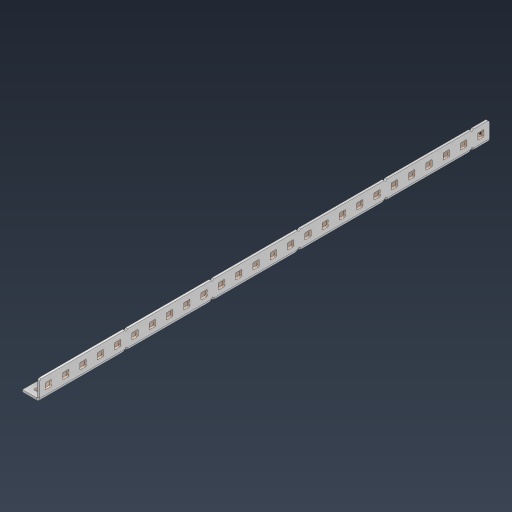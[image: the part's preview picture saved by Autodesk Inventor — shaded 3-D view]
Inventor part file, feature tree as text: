
AUTODESK INVENTOR PART (.ipt)
format: ipt  version: 2024.3 (Build 283343000, 343)  size: 1,030,656 bytes
history: native  units: in
note: dims shown in document units (in); Inventor stores cm internally (conversion verified against a paired STEP export)
features: other x85, extrude x76, sheet_metal_op x11, pattern_linear x2, mirror x1, chamfer x1, sketch x1
ambient origin geometry x8: Origin, YZ Plane, XZ Plane, XY Plane, X Axis, Y Axis, Z Axis, Center Point
bodies: Solid1 (feature_tree), Body (feature_tree)
feature tree (177):
  sheet_metal_op  "Flanges"
  other  "Flange Pattern Plane"
  other  "Flange Pattern Sketch"
  sheet_metal_op  "Flange Pattern"
  sheet_metal_op  "Body Pattern"
  pattern_linear  "Center Pattern"  Spacing1=13.0in  [1 undecoded]
  other  "Arc Length"
  mirror  "Notch Mirror"
  pattern_linear  "Notch Pattern"  Spacing1=0.0625in  [1 undecoded]
  chamfer  "End Chamfer"
  extrude  "Half Cut"  Depth=0.0625in
  other  "Plate1"
  sketch  "Sketch2"  dims[d0=1.0in d1=13.0in d2=0.0625in d3=0.0625in d4=0.0312in d5=0.125in d6=0.0625in d7=0.5in d8=90.0deg d9=0.0312in d10=0.25in d11=0.0625in d12=0.0625in d16=0.182in d17=0.02in d18=0.0625in d19=0.0in d20=0.25in d21=0.25in d38=10.2362in d40=0.5in d41=0.3937in d43=1.0in d46=0.172in d47=1.0in d48=0.0in d49=0.182in d50=0.02in d51=0.25in d52=0.25in d53=0.0625in d54=0.0in d55=0.172in d56=1.0in d57=0.0in d58=0.25in d60=10.2362in d62=0.5in d63=0.3937in d65=0.5in d85=0.1473in d86=0.1782in d88=0.04in d89=0.0625in d90=0.0in d91=0.04in d92=0.0491in d95=2.5in d96=0.04in d97=0.25in d98=45.0deg d99=0.25in d100=0.5in d101=0.0in d102=2.497in d106=0.182in d107=0.02in d108=0.5in d109=0.5in d110=0.0625in d111=0.0in d112=0.172in d113=0.5in d114=0.0in d117=0.5in d118=0.5in d119=0.5in]
  other  "Plate2"
  sheet_metal_op  "Bend1"
  sheet_metal_op  "Corner1"
  other  "Srf1"
  other  "Srf2"
  other  "Srf91"
  sheet_metal_op  "Body Pattern Sketch"
  other  "Srf92"
  other  "Srf786"
  other  "Srf823"
  other  "Srf824"
  other  "Srf825"
  other  "Srf826"
  other  "Srf827"
  other  "Srf828"
  other  "Srf829"
  other  "Srf856"
  other  "Srf857"
  other  "Srf858"
  other  "Srf859"
  other  "Srf860"
  other  "Srf861"
  other  "Srf862"
  other  "Srf889"
  other  "Srf890"
  other  "Srf891"
  other  "Srf892"
  other  "Srf893"
  other  "Srf894"
  other  "Srf895"
  other  "Srf896"
  other  "Srf922"
  other  "Srf923"
  other  "Srf924"
  other  "Srf925"
  other  "Srf926"
  other  "Srf959"
  other  "Srf960"
  other  "Srf961"
  other  "Srf962"
  other  "Srf963"
  other  "Srf996"
  other  "Srf997"
  other  "Srf998"
  other  "Srf999"
  other  "Srf1000"
  other  "Srf1143"
  other  "Srf1144"
  other  "Srf1145"
  other  "Srf1146"
  other  "Srf1147"
  other  "Srf1148"
  other  "Srf1149"
  other  "Srf1150"
  other  "Srf1151"
  other  "Srf1152"
  other  "Srf1153"
  other  "Srf1154"
  other  "Srf1199"
  other  "Srf1200"
  other  "Srf1201"
  other  "Srf1202"
  other  "Srf1203"
  other  "Srf1204"
  other  "Srf1205"
  other  "Srf1206"
  other  "Srf1207"
  other  "Srf1208"
  other  "Srf1209"
  other  "Srf1210"
  other  "Srf1255"
  other  "Srf1256"
  other  "Srf1257"
  other  "Srf1258"
  other  "Srf1259"
  other  "Srf1260"
  other  "Srf1261"
  other  "Srf1262"
  other  "Srf1263"
  other  "Srf1264"
  other  "Srf1265"
  other  "Srf1266"
  sheet_metal_op  "Flange Stamp"
  sheet_metal_op  "Flange Circle"
  sheet_metal_op  "Body Stamp"
  sheet_metal_op  "Body Circle"
  other  "Center Stamp"
  other  "Center Circle"
  sheet_metal_op  "Notch"
  extrude  "ExtrusionSrf2"  Depth=0.0312in
  extrude  "ExtrusionSrf92"  Depth=0.5in
  extrude  "ExtrusionSrf823"  Depth=0.0625in
  extrude  "ExtrusionSrf824"  Depth=0.5in TaperAngle=90.0deg
  extrude  "ExtrusionSrf825"  Depth=0.25in
  extrude  "ExtrusionSrf826"  Depth=0.0625in
  extrude  "ExtrusionSrf827"  Depth=0.0625in
  extrude  "ExtrusionSrf828"  Depth=0.182in
  extrude  "ExtrusionSrf829"  Depth=0.02in
  extrude  "ExtrusionSrf856"  Depth=0.0625in
  extrude  "ExtrusionSrf857"  TaperAngle=0.0deg  [1 undecoded]
  extrude  "ExtrusionSrf858"  Depth=0.25in
  extrude  "ExtrusionSrf859"  Depth=0.25in
  extrude  "ExtrusionSrf860"  Depth=0.5in
  extrude  "ExtrusionSrf861"  Depth=0.5in
  extrude  "ExtrusionSrf862"  Depth=1.0in TaperAngle=0.0deg
  extrude  "ExtrusionSrf889"  Depth=0.182in
  extrude  "ExtrusionSrf890"  Depth=0.02in
  extrude  "ExtrusionSrf891"  Depth=0.25in
  extrude  "ExtrusionSrf892"  Depth=0.25in
  extrude  "ExtrusionSrf893"  Depth=0.0625in
  extrude  "ExtrusionSrf894"  TaperAngle=0.0deg  [1 undecoded]
  extrude  "ExtrusionSrf895"  Depth=0.5in
  extrude  "ExtrusionSrf896"  Depth=1.0in TaperAngle=0.0deg
  extrude  "ExtrusionSrf922"  Depth=0.25in
  extrude  "ExtrusionSrf923"  Depth=0.5in
  extrude  "ExtrusionSrf924"  Depth=0.5in
  extrude  "ExtrusionSrf925"  Depth=0.5in
  extrude  "ExtrusionSrf926"  Depth=0.5in
  extrude  "ExtrusionSrf959"  Depth=0.5in
  extrude  "ExtrusionSrf960"  Depth=0.0625in
  extrude  "ExtrusionSrf961"  TaperAngle=0.0deg  [1 undecoded]
  extrude  "ExtrusionSrf962"  Depth=0.5in
  extrude  "ExtrusionSrf963"  Depth=0.5in
  extrude  "ExtrusionSrf996"  Depth=2.5in
  extrude  "ExtrusionSrf997"  Depth=0.25in TaperAngle=45.0deg
  extrude  "ExtrusionSrf998"  Depth=0.25in
  extrude  "ExtrusionSrf999"  Depth=0.5in TaperAngle=0.0deg
  extrude  "ExtrusionSrf1000"  Depth=0.5in
  extrude  "ExtrusionSrf1143"  Depth=0.182in
  extrude  "ExtrusionSrf1144"  Depth=0.02in
  extrude  "ExtrusionSrf1145"  Depth=0.5in
  extrude  "ExtrusionSrf1146"  Depth=0.5in
  extrude  "ExtrusionSrf1147"  Depth=0.0625in
  extrude  "ExtrusionSrf1148"  TaperAngle=0.0deg  [1 undecoded]
  extrude  "ExtrusionSrf1149"  Depth=0.5in
  extrude  "ExtrusionSrf1150"  Depth=0.5in TaperAngle=0.0deg
  extrude  "ExtrusionSrf1151"  Depth=0.5in
  extrude  "ExtrusionSrf1152"  Depth=0.5in
  extrude  "ExtrusionSrf1153"  Depth=0.5in
  extrude  "ExtrusionSrf1154"  [1 undecoded]
  extrude  "ExtrusionSrf1199"  [1 undecoded]
  extrude  "ExtrusionSrf1200"  [1 undecoded]
  extrude  "ExtrusionSrf1201"  [1 undecoded]
  extrude  "ExtrusionSrf1202"  [1 undecoded]
  extrude  "ExtrusionSrf1203"  [1 undecoded]
  extrude  "ExtrusionSrf1204"  [1 undecoded]
  extrude  "ExtrusionSrf1205"  [1 undecoded]
  extrude  "ExtrusionSrf1206"  [1 undecoded]
  extrude  "ExtrusionSrf1207"  [1 undecoded]
  extrude  "ExtrusionSrf1208"  [1 undecoded]
  extrude  "ExtrusionSrf1209"  [1 undecoded]
  extrude  "ExtrusionSrf1210"  [1 undecoded]
  extrude  "ExtrusionSrf1255"  [1 undecoded]
  extrude  "ExtrusionSrf1256"  [1 undecoded]
  extrude  "ExtrusionSrf1257"  [1 undecoded]
  extrude  "ExtrusionSrf1258"  [1 undecoded]
  extrude  "ExtrusionSrf1259"  [1 undecoded]
  extrude  "ExtrusionSrf1260"  [1 undecoded]
  extrude  "ExtrusionSrf1261"  [1 undecoded]
  extrude  "ExtrusionSrf1262"  [1 undecoded]
  extrude  "ExtrusionSrf1263"  [1 undecoded]
  extrude  "ExtrusionSrf1264"  [1 undecoded]
  extrude  "ExtrusionSrf1265"  [1 undecoded]
  extrude  "ExtrusionSrf1266"  [1 undecoded]
note: 31 required parameter values undecoded (feature->parameter linkage not recoverable at this tier; creation-order binding heuristic only, values carry confidence <= 0.55)
